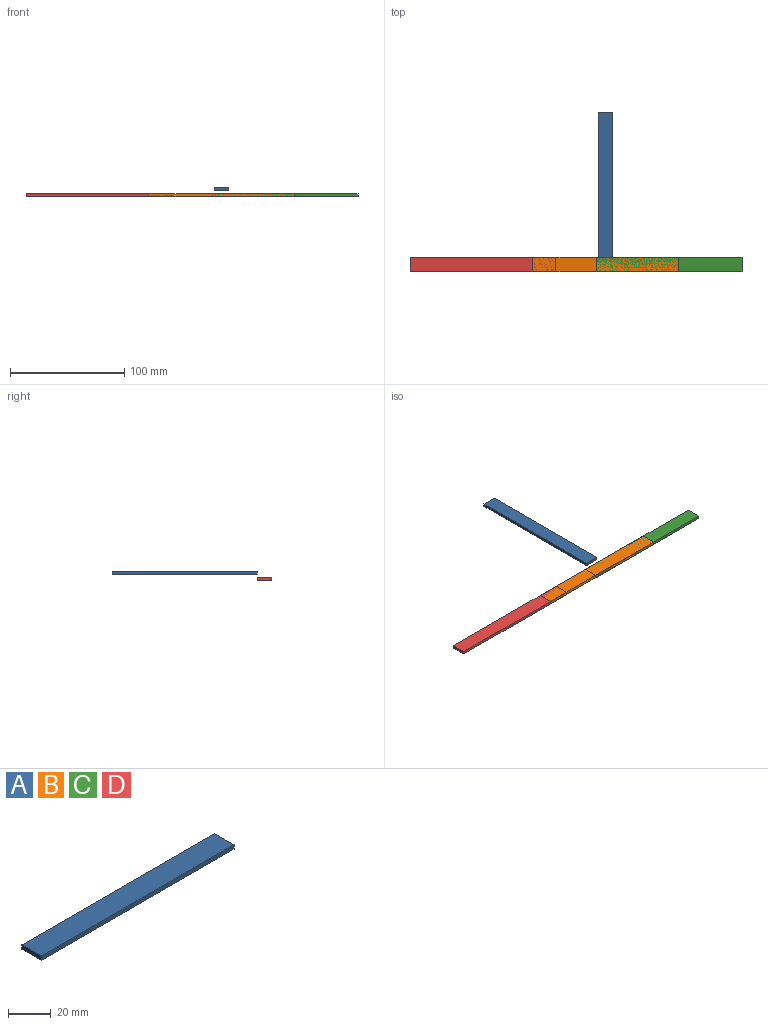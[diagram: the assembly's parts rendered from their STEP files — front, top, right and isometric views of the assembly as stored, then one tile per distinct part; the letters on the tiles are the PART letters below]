
ASSEMBLY  parts=4 mates=3
PART A: 6 faces, bbox 127x12.7x2.5 mm
  f0: plane 127x2.54mm, normal (0,1,0), area 322.6mm2, adj f1,f3,f4,f5
  f1: plane 12.7x2.54mm, normal (-1,0,0), area 32.3mm2, adj f0,f2,f4,f5
  f2: plane 127x2.54mm, normal (0,-1,0), area 322.6mm2, adj f1,f3,f4,f5
  f3: plane 12.7x2.54mm, normal (1,0,0), area 32.3mm2, adj f0,f2,f4,f5
  f4: plane 127x12.7mm, normal (0,0,1), area 1612.9mm2, adj f0,f1,f2,f3
  f5: plane 127x12.7mm, normal (0,0,-1), area 1612.9mm2, adj f0,f1,f2,f3
PART B: same geometry as A
PART C: same geometry as A
PART D: same geometry as A
PLACE A rot(axis=(0,0,1),90deg) t=(47.99,17.43,7.16)mm
PLACE B t=(-21.86,4.73,1.22)mm
PLACE C t=(33.99,4.73,1.22)mm
PLACE D t=(-129.43,4.73,1.22)mm
MATE slider C.f1 <-> B.f3  axis (-1,0,0) through (33.99,11.08,2.49)mm
MATE slider D.f3 <-> B.f1  axis (1,0,0) through (-2.43,11.08,2.49)mm
MATE slider A.f4 <-> B.f4  axis (0,0,1) through (41.64,17.43,9.7)mm
